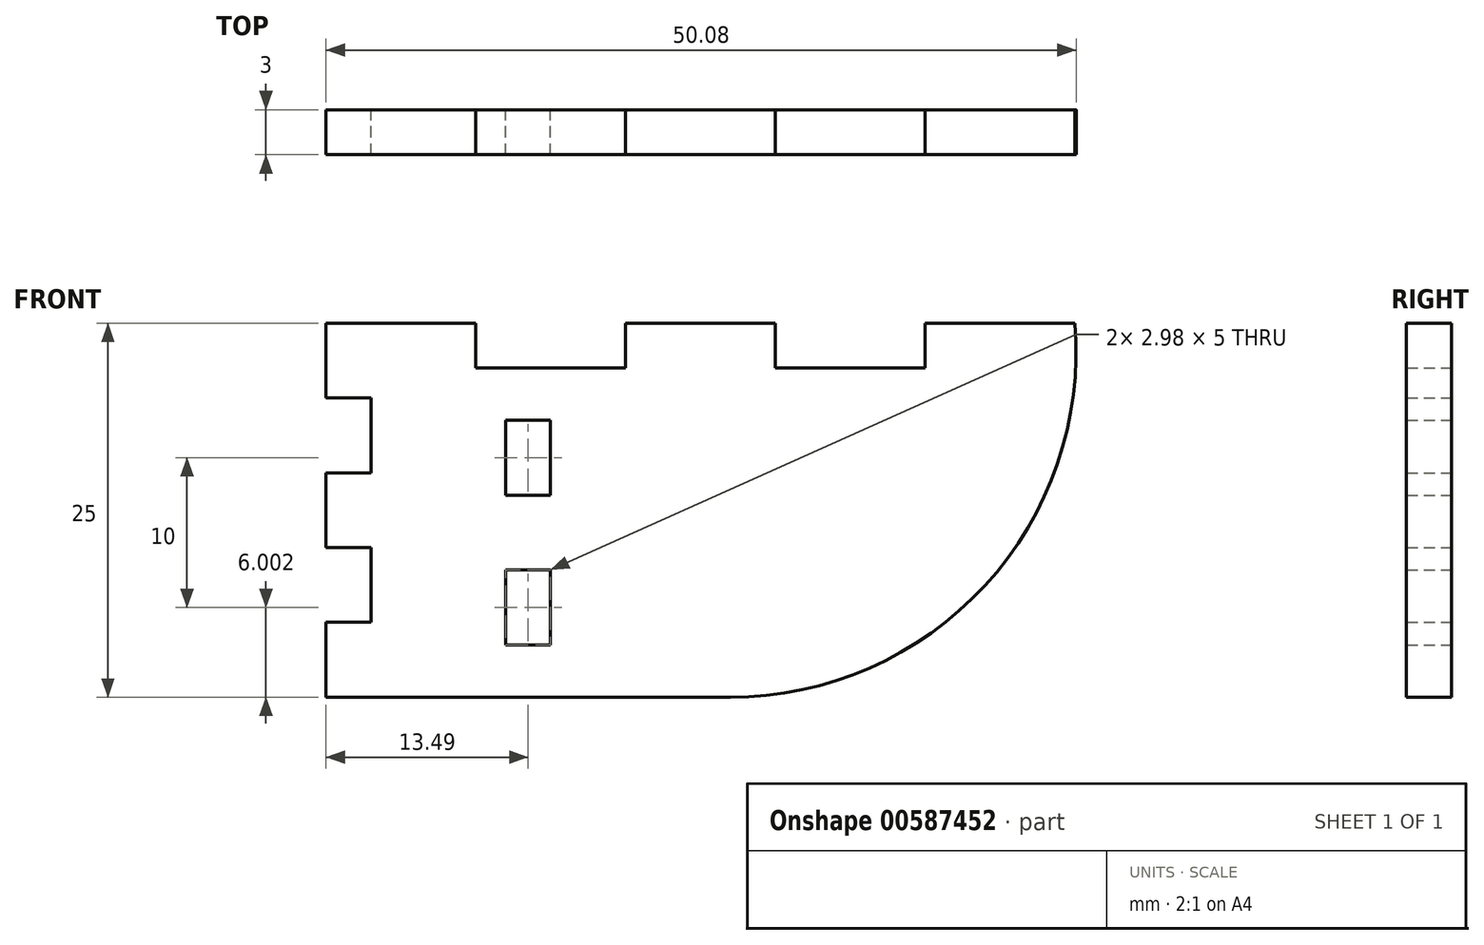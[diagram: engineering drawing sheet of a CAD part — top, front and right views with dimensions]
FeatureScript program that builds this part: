
annotation { "Feature Type Name" : "Feature", "Feature Type Description" : "" }
export const myFeature = defineFeature(function(context is Context, id is Id, definition is map)
    precondition{}
    {
        {
            var Q0;
            Q0=qCreatedBy(makeId("Front.planeOp"),FACE);
            var sketch = newSketch(context, id + "F0", { "sketchPlane" : qUnion([Q0])});
            skLineSegment(sketch, "E0", {"start": v(-63.57, 23.04) * mm, "end": v(-13.57, 23.04) * mm, "construction": true});
            skArc(sketch, "E1", {"start": v(-36.57, -1.96) * mm, "mid": v(-19.58, 5.5) * mm, "end": v(-13.57, 23.04) * mm});
            skLineSegment(sketch, "E2", {"start": v(-36.57, -1.96) * mm, "end": v(-63.57, -1.96) * mm});
            skLineSegment(sketch, "E3", {"start": v(-63.57, 23.04) * mm, "end": v(-63.57, -1.96) * mm, "construction": true});
            skLineSegment(sketch, "E4", {"start": v(-63.57, 23.04) * mm, "end": v(-53.57, 23.04) * mm});
            skLineSegment(sketch, "E5", {"start": v(-53.57, 23.04) * mm, "end": v(-53.57, 20.04) * mm});
            skLineSegment(sketch, "E6", {"start": v(-53.57, 20.04) * mm, "end": v(-43.57, 20.04) * mm});
            skLineSegment(sketch, "E7", {"start": v(-43.57, 20.04) * mm, "end": v(-43.57, 23.04) * mm});
            skLineSegment(sketch, "E8", {"start": v(-43.57, 23.04) * mm, "end": v(-33.57, 23.04) * mm});
            skLineSegment(sketch, "E9", {"start": v(-33.57, 23.04) * mm, "end": v(-33.57, 20.04) * mm});
            skLineSegment(sketch, "E10", {"start": v(-33.57, 20.04) * mm, "end": v(-23.57, 20.04) * mm});
            skLineSegment(sketch, "E11", {"start": v(-23.57, 20.04) * mm, "end": v(-23.57, 23.04) * mm});
            skLineSegment(sketch, "E12", {"start": v(-23.57, 23.04) * mm, "end": v(-13.57, 23.04) * mm});
            skLineSegment(sketch, "E13", {"start": v(-63.57, 23.04) * mm, "end": v(-63.57, 18.04) * mm});
            skLineSegment(sketch, "E14", {"start": v(-63.57, 18.04) * mm, "end": v(-60.57, 18.04) * mm});
            skLineSegment(sketch, "E15", {"start": v(-60.57, 18.04) * mm, "end": v(-60.57, 13.04) * mm});
            skLineSegment(sketch, "E16", {"start": v(-60.57, 13.04) * mm, "end": v(-63.57, 13.04) * mm});
            skLineSegment(sketch, "E17", {"start": v(-63.57, 13.04) * mm, "end": v(-63.57, 8.04) * mm});
            skLineSegment(sketch, "E18", {"start": v(-63.57, 8.04) * mm, "end": v(-60.57, 8.04) * mm});
            skLineSegment(sketch, "E19", {"start": v(-60.57, 8.04) * mm, "end": v(-60.57, 3.04) * mm});
            skLineSegment(sketch, "E20", {"start": v(-60.57, 3.04) * mm, "end": v(-63.57, 3.04) * mm});
            skLineSegment(sketch, "E21", {"start": v(-63.57, 3.04) * mm, "end": v(-63.57, -1.96) * mm});
            skLineSegment(sketch, "E22.bottom", {"start": v(-51.57, 1.54) * mm, "end": v(-48.59, 1.54) * mm});
            skLineSegment(sketch, "E22.top", {"start": v(-51.57, 6.54) * mm, "end": v(-48.59, 6.54) * mm});
            skLineSegment(sketch, "E22.left", {"start": v(-51.57, 1.54) * mm, "end": v(-51.57, 6.54) * mm});
            skLineSegment(sketch, "E22.right", {"start": v(-48.59, 1.54) * mm, "end": v(-48.59, 6.54) * mm});
            skLineSegment(sketch, "E23.bottom", {"start": v(-51.57, 11.54) * mm, "end": v(-48.59, 11.54) * mm});
            skLineSegment(sketch, "E23.top", {"start": v(-51.57, 16.54) * mm, "end": v(-48.59, 16.54) * mm});
            skLineSegment(sketch, "E23.left", {"start": v(-51.57, 11.54) * mm, "end": v(-51.57, 16.54) * mm});
            skLineSegment(sketch, "E23.right", {"start": v(-48.59, 11.54) * mm, "end": v(-48.59, 16.54) * mm});
            skSolve(sketch);
        }
        {
            var Q0;
            Q0 = qSketchRegion(id + "F0", true);
            extrude(context, id + "F1", {"entities" : qUnion([Q0]), "depth" : 3 * mm, "offsetDistance" : 25 * mm});
        }
    });
